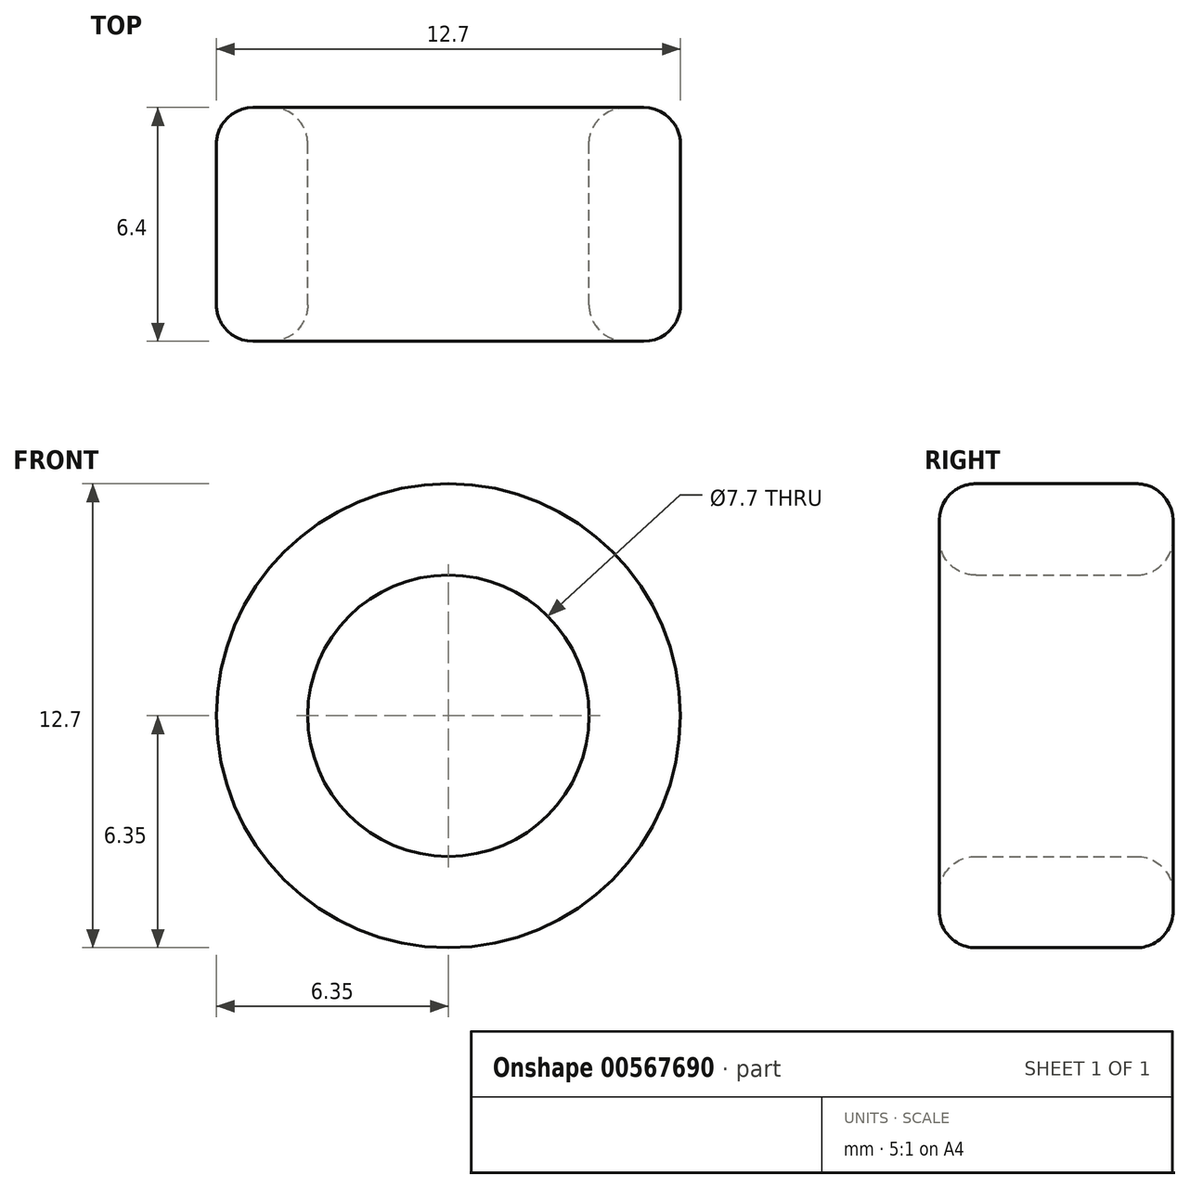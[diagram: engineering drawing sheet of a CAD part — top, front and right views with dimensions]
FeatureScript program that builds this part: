
annotation { "Feature Type Name" : "Feature", "Feature Type Description" : "" }
export const myFeature = defineFeature(function(context is Context, id is Id, definition is map)
    precondition{}
    {
        {
            var Q0;
            Q0=qCreatedBy(makeId("Front.planeOp"),FACE);
            var sketch = newSketch(context, id + "F0", { "sketchPlane" : qUnion([Q0])});
            skCircle(sketch, "E0", {"center": v(0, 6.7) * mm, "radius": 3.85 * mm});
            skCircle(sketch, "E1", {"center": v(0, 6.7) * mm, "radius": 6.35 * mm});
            skSolve(sketch);
        }
        {
            var Q0;
            Q0=makeQuery(id+"F0.imprint","IMPRINT",FACE,{"disambiguationData":[TD([[makeQuery(id+"F0.imprint","IMPRINT",EDGE,{"derivedFrom":sQuery(id+"F0.wireOp",EDGE,"E0")}),-1.0]])]});
            extrude(context, id + "F1", {"entities" : qUnion([Q0]), "endBound" : BoundingType.SYMMETRIC, "depth" : 6.4 * mm, "offsetDistance" : 25 * mm});
        }
        {
            var Q0;
            Q0=makeQuery(id+"F1.opExtrude","SWEPT_FACE",FACE,{"disambiguationData":[OSD([sQuery(id+"F0.wireOp",EDGE,"E1")])]});
            var Q1;
            Q1=makeQuery(id+"F1.opExtrude","SWEPT_FACE",FACE,{"disambiguationData":[OSD([sQuery(id+"F0.wireOp",EDGE,"E0")])]});
            fillet(context, id + "F2", {"entities" : qUnion([Q0, Q1]), "radius" : 1 * mm, "tangentPropagation" : true, "allowEdgeOverflow" : false});
        }
    });
